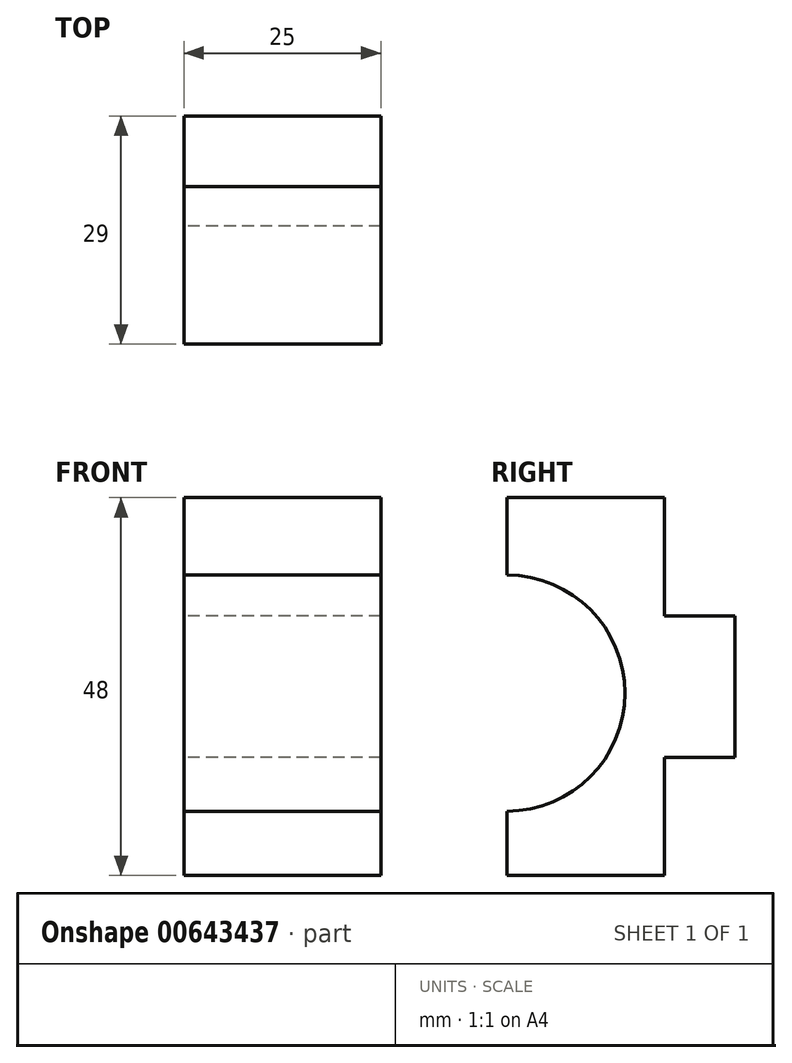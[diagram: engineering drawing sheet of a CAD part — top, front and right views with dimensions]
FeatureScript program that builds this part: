
annotation { "Feature Type Name" : "Feature", "Feature Type Description" : "" }
export const myFeature = defineFeature(function(context is Context, id is Id, definition is map)
    precondition{}
    {
        {
            var Q0;
            Q0=qCreatedBy(makeId("Right.planeOp"),FACE);
            var sketch = newSketch(context, id + "F0", { "sketchPlane" : qUnion([Q0])});
            skArc(sketch, "E0", {"start": v(0, -15) * mm, "mid": v(15, 0) * mm, "end": v(0, 15) * mm});
            skLineSegment(sketch, "E1", {"start": v(0, 15) * mm, "end": v(0, 24.83) * mm});
            skLineSegment(sketch, "E2", {"start": v(0, 24.83) * mm, "end": v(20, 24.83) * mm});
            skLineSegment(sketch, "E3", {"start": v(20, 24.83) * mm, "end": v(20, 9.83) * mm});
            skLineSegment(sketch, "E4", {"start": v(20, 9.83) * mm, "end": v(29, 9.83) * mm});
            skPoint(sketch, "E5.start.orphan", {"position": v(20, -4.53) * mm});
            skPoint(sketch, "E6.start.orphan", {"position": v(0, -19.71) * mm});
            skLineSegment(sketch, "E7", {"start": v(29, 9.83) * mm, "end": v(29, -8.17) * mm});
            skLineSegment(sketch, "E8", {"start": v(29, -8.17) * mm, "end": v(20, -8.17) * mm});
            skLineSegment(sketch, "E9", {"start": v(20, -8.17) * mm, "end": v(20, -23.17) * mm});
            skLineSegment(sketch, "E10", {"start": v(20, -23.17) * mm, "end": v(0, -23.17) * mm});
            skLineSegment(sketch, "E11", {"start": v(0, -23.17) * mm, "end": v(0, -15) * mm});
            skSolve(sketch);
        }
        {
            var Q0;
            Q0=makeQuery(id+"F0.imprint","IMPRINT",FACE,{"disambiguationData":[TD([[makeQuery(id+"F0.imprint","IMPRINT",EDGE,{"derivedFrom":sQuery(id+"F0.wireOp",EDGE,"E0")}),-1.0]])]});
            extrude(context, id + "F1", {"entities" : qUnion([Q0]), "depth" : 25 * mm, "offsetDistance" : 25 * mm});
        }
    });
